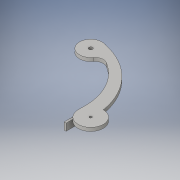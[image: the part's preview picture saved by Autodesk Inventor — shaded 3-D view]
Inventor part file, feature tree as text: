
AUTODESK INVENTOR PART (.ipt)
format: ipt  version: 2016 (Build 200138000, 138)  size: 144,896 bytes
history: native  units: in
note: dims shown in document units (in); Inventor stores cm internally (conversion verified against a paired STEP export)
features: sketch x9, other x3
ambient origin geometry x8: Origin, YZ Plane, XZ Plane, XY Plane, X Axis, Y Axis, Z Axis, Center Point
bodies: Solid1 (feature_tree)
feature tree (12):
  other  "Part4.ipt"
  other  "Solid1::Part4.ipt"
  other  "TaggingFeature1"
  sketch  "Sketch1"  dims[d0=0.3937in]
  sketch  "Sketch2"
  sketch  "Sketch3"
  sketch  "Sketch6"
  sketch  "Sketch7"
  sketch  "Sketch13"
  sketch  "Sketch16"
  sketch  "Sketch17"
  sketch  "Sketch18"
